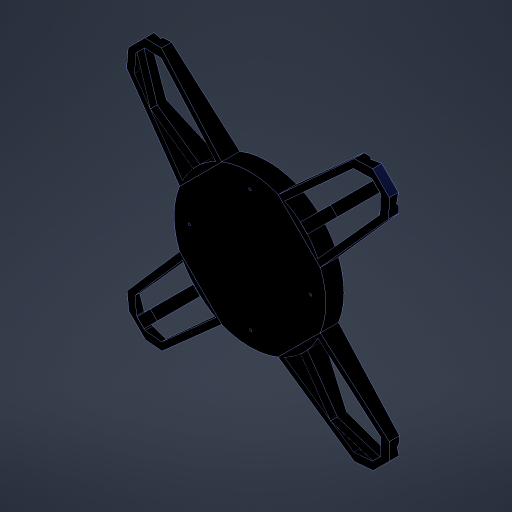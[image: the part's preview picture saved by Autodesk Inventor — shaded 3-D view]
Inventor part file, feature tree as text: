
AUTODESK INVENTOR PART (.ipt)
format: ipt  version: 2023 (Build 270158000, 158)  size: 621,056 bytes
history: native  units: mm
features: chamfer x20, extrude x7, sketch x7, fillet x3, pattern_circular x1, direct_edit x1, other x1
ambient origin geometry x8: Origin, YZ Plane, XZ Plane, XY Plane, X Axis, Y Axis, Z Axis, Center Point
bodies: Solid1 (feature_tree)
feature tree (40):
  extrude  "Extrusion1"  Depth=200.0mm
  fillet  "Fillet1"  Radius=30.0mm
  extrude  "Extrusion2"  Depth=30.0mm
  extrude  "Extrusion3"  Depth=30.0mm
  chamfer  "Chamfer1"  Distance=10.0mm
  extrude  "Extrusion4"  Depth=10.0mm
  chamfer  "Chamfer2"  Distance=15.0mm
  chamfer  "Chamfer3"  Angle=45.0deg  [1 undecoded]
  chamfer  "Chamfer4"  Distance=25.0mm
  chamfer  "Chamfer5"  Distance=85.0mm
  chamfer  "Chamfer6"  Distance=25.0mm
  chamfer  "Chamfer7"  Distance=85.0mm
  chamfer  "Chamfer8"  Distance=8.37758mm
  chamfer  "Chamfer9"  Distance=5.0mm
  extrude  "Extrusion5"  Depth=10.0mm TaperAngle=360.0deg
  pattern_circular  "Circular Pattern1"  [2 undecoded]
  chamfer  "Chamfer12"  Distance=7.5mm Angle=45.0deg
  chamfer  "Chamfer13"  Distance=40.0mm Angle=360.0deg
  chamfer  "Chamfer14"  Distance=20.0mm
  chamfer  "Chamfer15"  Distance=42.5mm Angle=45.0deg
  chamfer  "Chamfer18"  Distance=42.5mm Angle=45.0deg
  chamfer  "Chamfer19"  Distance=42.5mm Angle=45.0deg
  fillet  "Fillet2"  Radius=42.5mm
  fillet  "Fillet3"  Radius=32.44mm
  chamfer  "Chamfer20"  Distance=32.44mm Angle=45.0deg
  chamfer  "Chamfer21"  Distance=32.44mm Angle=45.0deg
  chamfer  "Chamfer22"  Distance=32.44mm Angle=45.0deg
  chamfer  "Chamfer23"  Distance=7.5mm
  chamfer  "Chamfer24"  Distance=8.1mm
  extrude  "Extrusion6"  Depth=10.0mm TaperAngle=360.0deg
  direct_edit  "Direct Edit2"
  extrude  "Extrusion7"  Depth=10.0mm TaperAngle=45.0deg
  sketch  "Sketch1"  dims[d0=200.0mm d1=200.0mm d2=30.0mm]
  sketch  "Sketch2"  dims[d3=30.0mm d4=30.0mm]
  sketch  "Sketch3"  dims[d5=30.0mm d6=30.0mm]
  sketch  "Sketch5"  dims[d7=30.0mm]
  sketch  "Sketch6"  dims[d8=30.0mm]
  sketch  "Sketch7"  dims[d9=30.0mm d10=10.0mm d11=0.0mm]
  sketch  "Sketch8"  dims[d12=10.0mm d13=125.0mm d14=15.0mm d15=0.0mm d16=45.0deg d17=25.0mm d18=85.0mm d20=25.0mm d21=85.0mm d22=8.37758mm d23=5.0mm d24=40.0mm d26=360.0deg d28=15.0mm d29=0.0mm d30=85.0mm d31=7.5mm d32=45.0deg d33=40.0mm d35=360.0deg d37=20.0mm d38=0.0mm d39=42.5mm d40=5.3mm d41=45.0deg d42=42.5mm d43=5.3mm d44=45.0deg d45=42.5mm d46=5.3mm d47=45.0deg d48=42.5mm d49=5.3mm d50=45.0deg d51=32.44mm d52=12.0mm d53=45.0deg d54=32.44mm d55=12.0mm d56=45.0deg d57=32.44mm d58=12.0mm d59=45.0deg d60=32.44mm d61=12.0mm d62=45.0deg d63=7.5mm d64=8.1mm d65=0.0mm d72=40.0mm d73=360.0deg d75=1.669mm d76=5.0mm d77=45.0deg d78=1.669mm d79=5.0mm d80=45.0deg d81=1.669mm d82=5.0mm d83=45.0deg d84=1.669mm d85=5.0mm d86=45.0deg d93=1.669mm d94=5.0mm d95=45.0deg d96=1.669mm d97=5.0mm d98=45.0deg d99=7.0mm d100=6.735mm d101=10.0mm d102=5.0mm d103=45.0deg d104=1.5mm d105=5.0mm d106=45.0deg d107=1.669mm d108=5.0mm d109=45.0deg d110=1.669mm d111=5.0mm d112=45.0deg d113=10.0mm d114=5.0mm d115=45.0deg d116=200.0mm d117=0.0mm d124=15.0mm d125=10.0mm d126=10.0mm d128=3.0mm d129=3.0mm d130=3.0mm d131=3.0mm d132=200.0mm d133=0.0mm d66=0.5mm d67=0.872665mm]
  other  "Scale2"
note: 3 required parameter values undecoded (feature->parameter linkage not recoverable at this tier; creation-order binding heuristic only, values carry confidence <= 0.55)
